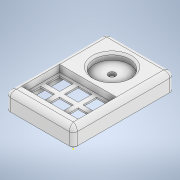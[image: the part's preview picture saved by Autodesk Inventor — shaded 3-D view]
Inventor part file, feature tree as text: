
AUTODESK INVENTOR PART (.ipt)
format: ipt  version: 2022 (Build 260153000, 153)  size: 463,360 bytes
history: native  units: in
note: dims shown in document units (in); Inventor stores cm internally (conversion verified against a paired STEP export)
features: sketch x12, extrude x11, fillet x3, chamfer x2
ambient origin geometry x8: Origin, YZ Plane, XZ Plane, XY Plane, X Axis, Y Axis, Z Axis, Center Point
bodies: Solid1 (feature_tree)
feature tree (28):
  extrude  "Extrusion1"  Depth=3.937in
  extrude  "Extrusion2"  Depth=1.4961in
  extrude  "Extrusion3"  Depth=0.3937in
  extrude  "Extrusion4"  Depth=0.5394in
  extrude  "Extrusion5"  Depth=0.5394in
  extrude  "Extrusion6"  Depth=0.5394in
  extrude  "Extrusion7"  Depth=0.5394in
  fillet  "Fillet4"  Radius=0.5394in
  extrude  "Extrusion9"  Depth=0.0591in TaperAngle=0.0deg
  extrude  "Extrusion10"  Depth=0.2598in TaperAngle=0.0deg
  extrude  "Extrusion11"  Depth=1.315in
  fillet  "Fillet5"  Radius=0.2677in
  extrude  "Extrusion12"  Depth=1.1083in
  sketch  "Sketch16"  dims[d44=0.1575in d45=0.1575in d46=0.3819in d47=0.0in d48=0.1575in d49=0.1575in d50=2.5118in d51=3.7795in d52=0.0787in d53=0.0591in d54=0.0709in d55=0.0in d63=0.0591in d64=0.189in d65=0.189in d66=0.189in d67=0.189in d69=0.2028in d70=0.311in d71=0.0in d72=0.1339in d73=0.1339in d74=0.1339in d75=0.1339in d76=0.0551in d77=0.0551in d78=0.0551in d79=0.0551in d80=0.1063in d81=0.1063in d82=0.1063in d83=0.1063in d84=0.1063in d85=0.1063in d86=0.1063in d87=0.1063in d88=0.2165in d89=0.0in d90=0.7874in d91=0.0787in d92=0.0in d101=0.1575in d110=0.1142in d111=0.1142in d112=0.1181in d113=0.0787in d114=0.1969in d115=0.0591in d116=0.0787in d117=0.0in d118=0.2028in d134=0.0197in d135=0.0787in d136=45.0deg d137=0.0787in d138=0.0787in d139=45.0deg d56=0.0197in d57=0.0344in d58=0.0197in d59=0.0344in]
  fillet  "Fillet6"  Radius=0.3307in
  chamfer  "Chamfer3"  Distance=0.1575in
  chamfer  "Chamfer4"  Distance=0.3819in
  sketch  "Sketch1"  dims[d0=2.6299in d1=3.937in]
  sketch  "Sketch2"  dims[d2=0.7087in d3=0.0in d6=1.4961in]
  sketch  "Sketch3"  dims[d7=0.2028in d8=0.3937in]
  sketch  "Sketch4"  dims[d9=0.2677in d10=0.0in d12=0.5394in]
  sketch  "Sketch7"  dims[d13=0.5394in d14=0.5394in]
  sketch  "Sketch8"  dims[d15=0.5394in d16=0.5394in]
  sketch  "Sketch10"  dims[d17=0.5394in d18=0.5394in d19=0.5394in]
  sketch  "Sketch12"  dims[d26=0.5394in d27=0.0591in d28=0.0in]
  sketch  "Sketch13"  dims[d30=1.378in d33=0.2598in d34=0.0in]
  sketch  "Sketch14"  dims[d35=2.8287in d36=1.315in d37=0.2677in]
  sketch  "Sketch15"  dims[d38=1.315in d39=1.1083in d40=0.3307in d41=0.0in]
